# Revit family: HVAC_Fireplaces_Regency-Fireplace_Studio-electric-fireplace_ES105-ES135-ES165
name_source: partatom
category: Specialty Equipment
units: mm (PartAtom-declared; Revit-internal decimal feet)

## family parameters
Classification Number = 23.40.20.34.14
Cut with Voids When Loaded = No
Enable Cutting in Views = No
Host = Face
Maintain Annotation Orientation = No
Part Type = Normal
Room Calculation Point = No
Round Connector Dimension = Use Diameter
Shared = No

## types (3) — shared parameters
Apparent Load = 1500 VA
Default Elevation = 48 "
Depth = 8 "
Description = The Studio provides all of these features and so much more to create the perfect ambience at just the touch of a button, with or without the heat.
Frequency = 60 Hz
Height = 13 "
Housing Material = Regency Fireplace - Metal - Black
Manufacturer = Regency Fireplace
Number of Poles = 1
Power Consumption = 1500 W
Power Factor = 1
Product Documentation Link = https://assets.regency-fire.com
Product Page URL = https://www.regency-fire.com
Product data url = https://www.bimobject.com
URL = https://www.regency-fire.com
Voltage = 120 V
zero-valued in all types: Version

## per-type parameters (varying)
| type | Frame | Width |
| ES105 | 44 " | 41 " |
| ES135 | 56 " | 53 " |
| ES165 | 65 " | 65 " |

note: column(s) folded — value = type name in every type: Model

## geometry (parser evidence)
native form markers: Sweep x2
no freeform markers — native parametric forms only
